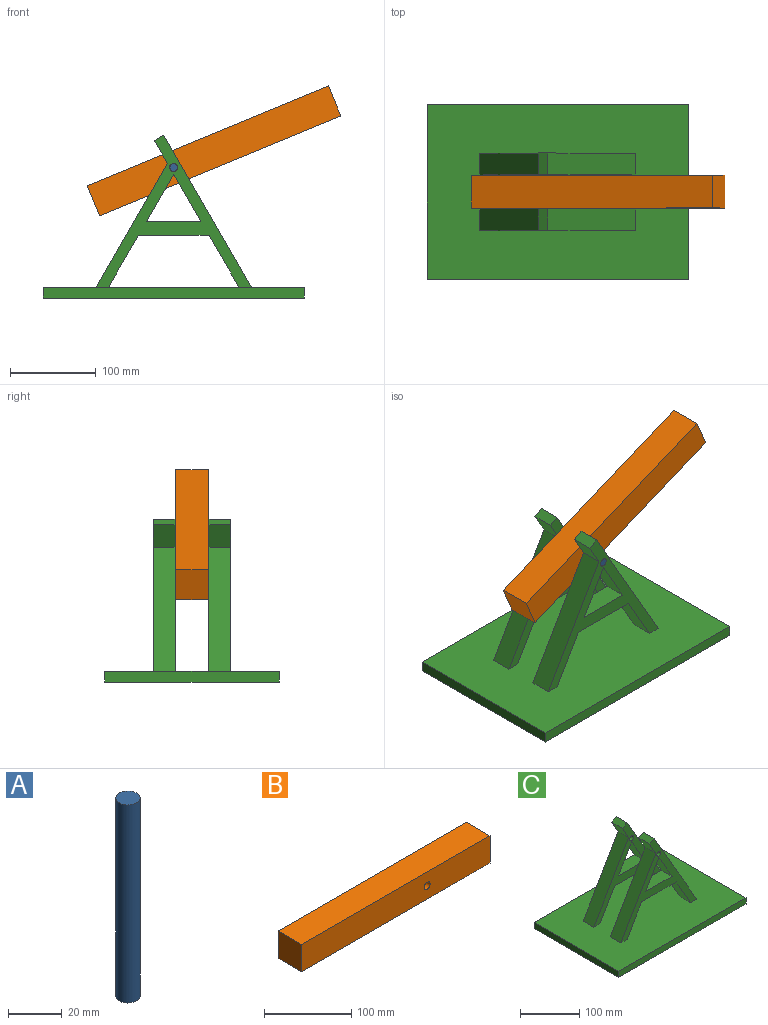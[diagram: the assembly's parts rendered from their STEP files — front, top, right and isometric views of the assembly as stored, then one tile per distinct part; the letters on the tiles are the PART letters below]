
ASSEMBLY  parts=3 mates=2
PART A: 3 faces, bbox 9x9x90.4 mm
  f0: plane 9.05x9.05mm, normal (0,0,-1), area 64.3mm2, adj f2
  f1: plane 9.05x9.05mm, normal (0,0,1), area 64.3mm2, adj f2
  f2: cylinder r=4.52mm len=90.42mm, axis (0,0,-1), area 2570.5mm2, adj f0,f1
PART B: 7 faces, bbox 304.8x38.1x38.1 mm
  f0: plane 304.8x38.1mm, normal (0,0,1), area 11612.9mm2, adj f1,f3,f4,f5
  f1: plane 38.1x38.1mm, normal (-1,0,0), area 1451.6mm2, adj f0,f2,f4,f5
  f2: plane 304.8x38.1mm, normal (0,0,-1), area 11612.9mm2, adj f1,f3,f4,f5
  f3: plane 38.1x38.1mm, normal (1,0,0), area 1451.6mm2, adj f0,f2,f4,f5
  f4: plane 304.8x38.1mm, normal (0,-1,0), area 11541.6mm2, adj f0,f1,f2,f3,f6
  f5: plane 304.8x38.1mm, normal (0,1,0), area 11541.6mm2, adj f0,f1,f2,f3,f6
  f6: cylinder r=4.76mm len=38.1mm, axis (0,-1,0), area 1140.1mm2, adj f4,f5
PART C: 32 faces, bbox 304.8x203.2x190.1 mm
  f0: plane 60.49x34.93mm, normal (0.87,0,-0.5), area 1774.2mm2, adj f12,f14,f21,f24
  f1: plane 60.49x34.93mm, normal (0.87,0,-0.5), area 1774.2mm2, adj f13,f14,f20,f23
  f2: plane 60.49x34.93mm, normal (-0.87,0,-0.5), area 1774.2mm2, adj f12,f14,f21,f24
  f3: plane 60.49x34.93mm, normal (-0.87,0,-0.5), area 1774.2mm2, adj f13,f14,f20,f23
  f4: plane 177.43x102.44mm, normal (0.87,0,0.5), area 5203.8mm2, adj f6,f14,f21,f24
  f5: plane 177.43x102.44mm, normal (0.87,0,0.5), area 5203.8mm2, adj f7,f14,f20,f23
  f6: plane 25.4x11mm, normal (-0.5,0,0.87), area 322.6mm2, adj f4,f8,f21,f24
  f7: plane 25.4x11mm, normal (-0.5,0,0.87), area 322.6mm2, adj f5,f9,f20,f23
  f8: plane 26.4x25.4mm, normal (-0.87,0,-0.5), area 774.1mm2, adj f6,f10,f21,f24
  f9: plane 26.4x25.4mm, normal (-0.87,0,-0.5), area 774.1mm2, adj f7,f11,f20,f23
  f10: plane 144.68x83.53mm, normal (-0.87,0,0.5), area 4243.4mm2, adj f8,f14,f21,f24
  f11: plane 144.68x83.53mm, normal (-0.87,0,0.5), area 4243.4mm2, adj f9,f14,f20,f23
  f12: plane 82.55x25.4mm, normal (0,0,-1), area 2096.8mm2, adj f0,f2,f21,f24
  f13: plane 82.55x25.4mm, normal (0,0,-1), area 2096.8mm2, adj f1,f3,f20,f23
  f14: plane 304.8x203.2mm, normal (0,0,1), area 60445.4mm2, adj f0,f1,f2,f3,f4,f5,f10,f11
  f15: plane 203.2x12.7mm, normal (-1,0,0), area 2580.6mm2, adj f14,f16,f18,f19
  f16: plane 304.8x203.2mm, normal (0,0,-1), area 61935.4mm2, adj f15,f17,f18,f19
  f17: plane 203.2x12.7mm, normal (1,0,0), area 2580.6mm2, adj f14,f16,f18,f19
  f18: plane 304.8x12.7mm, normal (0,-1,0), area 3871mm2, adj f14,f15,f16,f17
  f19: plane 304.8x12.7mm, normal (0,1,0), area 3871mm2, adj f14,f15,f16,f17
  f20: plane 181.73x177.43mm, normal (0,-1,0), area 5717.5mm2, adj f1,f3,f5,f7,f9,f11,f13,f14
  f21: plane 181.73x177.43mm, normal (0,1,0), area 5717.5mm2, adj f0,f2,f4,f6,f8,f10,f12,f14
  f22: cylinder r=4.76mm len=25.4mm, axis (0,-1,0), area 760.1mm2, adj f20,f23
  f23: plane 181.73x177.43mm, normal (0,1,0), area 5717.5mm2, adj f1,f3,f5,f7,f9,f11,f13,f14
  f24: plane 181.73x177.43mm, normal (0,-1,0), area 5717.5mm2, adj f0,f2,f4,f6,f8,f10,f12,f14
  f25: plane 63.5x25.4mm, normal (0,0,1), area 1612.9mm2, adj f21,f24,f26,f27
  f26: plane 54.99x31.75mm, normal (0.87,0,-0.5), area 1612.9mm2, adj f21,f24,f25,f27
  f27: plane 54.99x31.75mm, normal (-0.87,0,-0.5), area 1612.9mm2, adj f21,f24,f25,f26
  f28: plane 63.5x25.4mm, normal (0,0,1), area 1612.9mm2, adj f20,f23,f29,f30
  f29: plane 54.99x31.75mm, normal (0.87,0,-0.5), area 1612.9mm2, adj f20,f23,f28,f30
  f30: plane 54.99x31.75mm, normal (-0.87,0,-0.5), area 1612.9mm2, adj f20,f23,f28,f29
  f31: cylinder r=4.76mm len=25.4mm, axis (0,-1,0), area 760.1mm2, adj f21,f24
PLACE A rot(axis=(0.61,-0.56,0.56),117.4deg) t=(0,45.21,152.36)mm
PLACE B rot(axis=(0,1,0),157.5deg) t=(0,0,152.36)mm
PLACE C t=(0,0,12.7)mm
MATE revolute A.f2 <-> B.f6  axis (0,1,0) through (0,0,152.36)mm
MATE revolute C.f22 <-> A.f2  axis (0,-1,0) through (0,-45.21,152.36)mm
